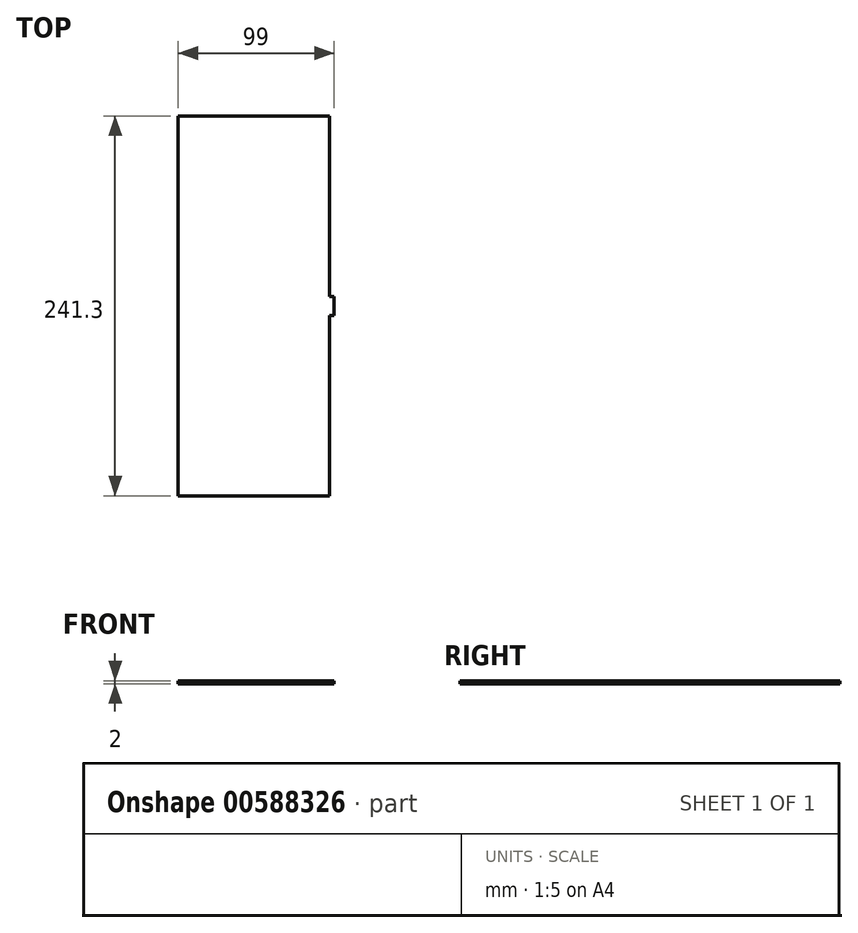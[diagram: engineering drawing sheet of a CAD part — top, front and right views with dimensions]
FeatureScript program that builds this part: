
annotation { "Feature Type Name" : "Feature", "Feature Type Description" : "" }
export const myFeature = defineFeature(function(context is Context, id is Id, definition is map)
    precondition{}
    {
        {
            var Q0;
            Q0=qCreatedBy(makeId("Right.planeOp"),FACE);
            var sketch = newSketch(context, id + "F0", { "sketchPlane" : qUnion([Q0])});
            skLineSegment(sketch, "E0", {"start": v(197.4, 98.54) * mm, "end": v(303.05, 98.54) * mm});
            skLineSegment(sketch, "E1", {"start": v(161.4, 98.54) * mm, "end": v(55.75, 98.54) * mm});
            skLineSegment(sketch, "E2", {"start": v(161.4, 98.54) * mm, "end": v(173.4, 98.54) * mm});
            skLineSegment(sketch, "E3", {"start": v(173.4, 98.54) * mm, "end": v(185.4, 98.54) * mm});
            skLineSegment(sketch, "E4", {"start": v(185.4, 98.54) * mm, "end": v(185.4, 76.54) * mm});
            skLineSegment(sketch, "E5", {"start": v(185.4, 76.54) * mm, "end": v(173.4, 76.54) * mm});
            skLineSegment(sketch, "E6", {"start": v(173.4, 76.54) * mm, "end": v(173.4, 98.54) * mm});
            skLineSegment(sketch, "E7", {"start": v(185.4, 76.54) * mm, "end": v(185.4, 74.54) * mm});
            skLineSegment(sketch, "E8", {"start": v(173.4, 76.54) * mm, "end": v(173.4, 74.54) * mm});
            skLineSegment(sketch, "E9", {"start": v(173.4, 74.54) * mm, "end": v(185.4, 74.54) * mm});
            skLineSegment(sketch, "E10", {"start": v(185.4, 76.54) * mm, "end": v(308.91, 76.54) * mm});
            skLineSegment(sketch, "E11", {"start": v(173.4, 76.54) * mm, "end": v(50.51, 76.54) * mm});
            skLineSegment(sketch, "E12", {"start": v(303.05, 98.54) * mm, "end": v(303.05, 76.54) * mm});
            skLineSegment(sketch, "E13", {"start": v(303.05, 76.54) * mm, "end": v(303.05, 74.54) * mm});
            skLineSegment(sketch, "E14", {"start": v(303.05, 74.54) * mm, "end": v(185.4, 74.54) * mm});
            skLineSegment(sketch, "E15", {"start": v(55.75, 98.54) * mm, "end": v(55.75, 76.54) * mm});
            skLineSegment(sketch, "E16", {"start": v(55.75, 76.54) * mm, "end": v(55.75, 74.54) * mm});
            skLineSegment(sketch, "E17", {"start": v(55.75, 74.54) * mm, "end": v(173.4, 74.54) * mm});
            skSolve(sketch);
        }
        {
            var Q0;
            {var subQ0=sQuery(id+"F0.wireOp",EDGE,"E7");Q0=makeQuery(id+"F0.imprint","IMPRINT",FACE,{"disambiguationData":[TD([[makeQuery(id+"F0.imprint","IMPRINT",EDGE,{"derivedFrom":subQ0}),1.0]])]});}
            var Q1;
            Q1=makeQuery(id+"F0.imprint","IMPRINT",FACE,{"disambiguationData":[TD([[makeQuery(id+"F0.imprint","IMPRINT",EDGE,{"derivedFrom":sQuery(id+"F0.wireOp",EDGE,"E5")}),1.0]])]});
            var Q2;
            {var subQ0=sQuery(id+"F0.wireOp",EDGE,"E8");Q2=makeQuery(id+"F0.imprint","IMPRINT",FACE,{"disambiguationData":[TD([[makeQuery(id+"F0.imprint","IMPRINT",EDGE,{"derivedFrom":subQ0}),-1.0]])]});}
            extrude(context, id + "F1", {"entities" : qUnion([Q0, Q1, Q2]), "oppositeDirection" : true, "depth" : 96 * mm, "offsetDistance" : 25 * mm});
        }
        {
            var Q0;
            Q0=makeQuery(id+"F0.imprint","IMPRINT",FACE,{"disambiguationData":[TD([[makeQuery(id+"F0.imprint","IMPRINT",EDGE,{"derivedFrom":sQuery(id+"F0.wireOp",EDGE,"E5")}),1.0]])]});
            extrude(context, id + "F2", {"entities" : qUnion([Q0]), "operationType" : NewBodyOperationType.ADD, "depth" : 3 * mm, "offsetDistance" : 25 * mm});
        }
        {
            var Q0;
            Q0=makeQuery(id+"F1.opExtrude","SWEPT_FACE",FACE,{"disambiguationData":[OSD([sQuery(id+"F0.wireOp",EDGE,"E16")])]});
            extrude(context, id + "F3", {"entities" : qUnion([Q0]), "operationType" : NewBodyOperationType.REMOVE, "oppositeDirection" : true, "depth" : 2 * mm, "offsetDistance" : 25 * mm});
        }
        {
            var Q0;
            Q0=makeQuery(id+"F1.opExtrude","SWEPT_FACE",FACE,{"disambiguationData":[OSD([sQuery(id+"F0.wireOp",EDGE,"E13")])]});
            extrude(context, id + "F4", {"entities" : qUnion([Q0]), "operationType" : NewBodyOperationType.REMOVE, "oppositeDirection" : true, "depth" : 2 * mm, "offsetDistance" : 25 * mm});
        }
        {
            var Q0;
            Q0=makeQuery(id+"F3.boolean.opBoolean","COPY",FACE,{"derivedFrom":makeQuery(id+"F3.opExtrude","CAP_FACE",FACE,{"disambiguationData":[OSD([sQuery(id+"F0.wireOp",EDGE,"E16")])],"isStart":false})});
            extrude(context, id + "F5", {"entities" : qUnion([Q0]), "operationType" : NewBodyOperationType.REMOVE, "oppositeDirection" : true, "depth" : 1 * mm, "offsetDistance" : 25 * mm});
        }
        {
            var Q0;
            Q0=makeQuery(id+"F4.boolean.opBoolean","COPY",FACE,{"derivedFrom":makeQuery(id+"F4.opExtrude","CAP_FACE",FACE,{"disambiguationData":[OSD([sQuery(id+"F0.wireOp",EDGE,"E13")])],"isStart":false})});
            extrude(context, id + "F6", {"entities" : qUnion([Q0]), "operationType" : NewBodyOperationType.REMOVE, "oppositeDirection" : true, "depth" : 1 * mm, "offsetDistance" : 25 * mm});
        }
    });
